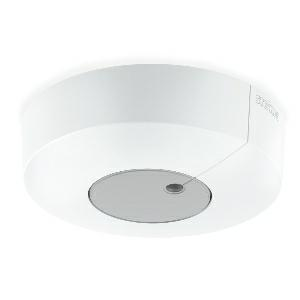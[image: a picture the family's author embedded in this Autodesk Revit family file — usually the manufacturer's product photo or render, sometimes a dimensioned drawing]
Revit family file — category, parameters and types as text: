
# Revit family: light_sensor_dual_057428
name_source: partatom
category: Elektroinstallationen
revit_build: Autodesk Revit 2016 (Build: 20190508_0715(x64)
units: mm (PartAtom-declared; Revit-internal decimal feet)

## family parameters
Basisbauteil = Fläche
Beim Laden mit Abzugskörper schneiden = Nein
Bemaßung runder Anschluss = Durchmesser verwenden
Beschriftungsausrichtung beibehalten = Nein
Gemeinsam genutzt = Nein
Raumberechnungspunkt = Nein
Teiletyp = Normal

## types (1)
- Light Sensor Dual
    Apparent Load = 0 VA
    Beschreibung = Type: Constant-lighting controller; Dimensions (Ø x H): 126 x 56 mm; Mains power supply: 12 – 22,5 V; Sensor Technology: Light sensor; Application, place: Outdoors, Indoors; Application, room: classroom, one-person office, open-plan office, high-bay warehouse, conference room / meeting room, Indoors; Installation site: wall, ceiling; Installation: Surface wiring; Mounting height: 2,00 – 4,00 m; Twilight setting TEACH: Yes; Twilight setting: 2 – 1000 lx; Control output, Dali: Addressable/slave; Basic light level function: No; Settings via: Bus; Interconnection: Yes; IP-rating: IP54; Material: Plastic; Ambient temperature: -20 – 50 °C; Colour: white; Colour, RAL: 9003; Manufacturer's Warranty: 5 years; Version: DALI-2 IPD - surface, rd.; PU1, EAN: 4007841057428
    Height = 0 mm  [stored 0 ft]
    Hersteller = Steinel
    Length = 126 mm
    ModVariant = Nein
    Modell = 057428
    Mounting Type = Surface mounted
    Number of Poles = 1
    OnlyDefault = Ja
    Power Factor = 1
    Product Name = Light Sensor Dual
    Product group = Sensor-switched indoor light
    ProductGroupID = 30
    Protection Class = Protection class
    Protection Degree = IP 54
    RlxData = <blob elided: 24861 chars, md5=f4920fe0>
    SensorDataFile = {"IESDataFiles":[]}
    Typenbild = produkt1_057428.jpg
    Typenkommentare = Product without accessories
    URL = http://relux.com
    VarID = ---
    Voltage = 0 V
    Vorgabe-Ansicht = 1800 mm
    Weight = 0.00 kg
    Width = 0 mm  [stored 0 ft]

note: [stored X ft] marks values corroborated as IEEE doubles in the binary element streams (Revit-internal decimal feet)

## geometry (parser evidence)
native form markers: Blend x4, Sweep x14
no freeform markers — native parametric forms only
